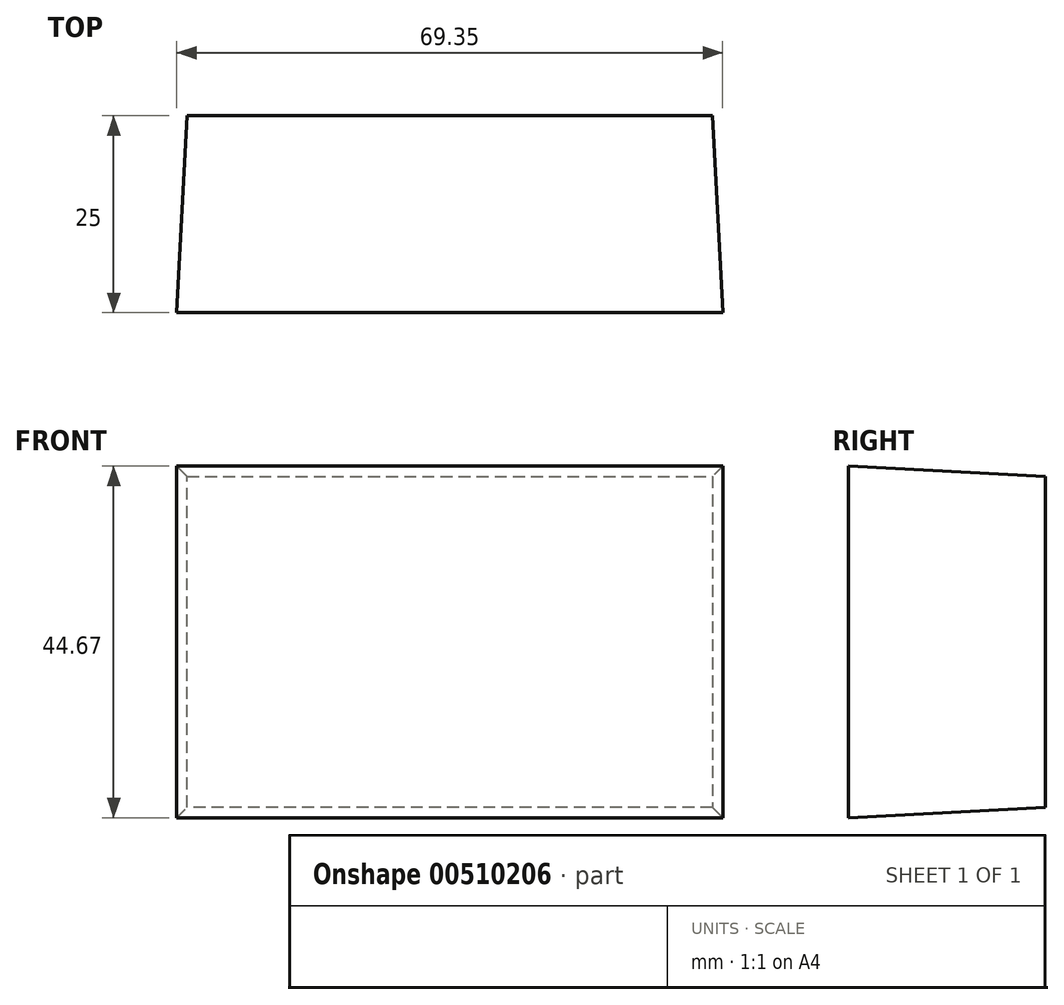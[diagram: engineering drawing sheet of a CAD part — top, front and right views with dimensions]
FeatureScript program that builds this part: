
annotation { "Feature Type Name" : "Feature", "Feature Type Description" : "" }
export const myFeature = defineFeature(function(context is Context, id is Id, definition is map)
    precondition{}
    {
        {
            var Q0;
            Q0=qCreatedBy(makeId("Front.planeOp"),FACE);
            var sketch = newSketch(context, id + "F0", { "sketchPlane" : qUnion([Q0])});
            skLineSegment(sketch, "E0.bottom", {"start": v(-22.97, 24.78) * mm, "end": v(43.76, 24.78) * mm});
            skLineSegment(sketch, "E0.top", {"start": v(-22.97, -17.27) * mm, "end": v(43.76, -17.27) * mm});
            skLineSegment(sketch, "E0.left", {"start": v(-22.97, 24.78) * mm, "end": v(-22.97, -17.27) * mm});
            skLineSegment(sketch, "E0.right", {"start": v(43.76, 24.78) * mm, "end": v(43.76, -17.27) * mm});
            skSolve(sketch);
        }
        {
            var Q0;
            Q0 = qSketchRegion(id + "F0", true);
            extrude(context, id + "F1", {"entities" : qUnion([Q0]), "depth" : 25 * mm, "hasDraft" : true, "draftAngle" : 3 * degree});
        }
    });
